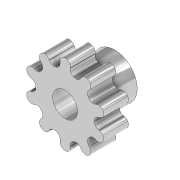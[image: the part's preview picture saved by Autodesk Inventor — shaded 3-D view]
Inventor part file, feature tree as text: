
AUTODESK INVENTOR PART (.ipt)
format: ipt  version: 2020 (Build 240168000, 168)  size: 233,984 bytes
history: native  units: in
note: dims shown in document units (in); Inventor stores cm internally (conversion verified against a paired STEP export)
features: extrude x3, sketch x3
ambient origin geometry x8: Origin, YZ Plane, XZ Plane, XY Plane, X Axis, Y Axis, Z Axis, Center Point
bodies: Body1 (feature_tree)
feature tree (6):
  extrude  "Extrusion4"  Depth=0.1969in
  extrude  "Extrusion5"  Depth=0.0866in
  extrude  "Extrusion6"  Depth=0.1969in
  sketch  "Sketch4"  dims[d1=0.563in d2=0.0866in d19=0.1969in]
  sketch  "Sketch5"  dims[d20=0.6378in d21=0.0866in]
  sketch  "Sketch6"  dims[d22=0.0827in d23=0.0827in d24=0.0827in d25=3.937in d27=360.0deg d29=0.1969in d30=0.0in d31=0.0787in d32=0.1969in d33=0.0in d34=0.0787in d35=0.1969in d36=0.0in]
